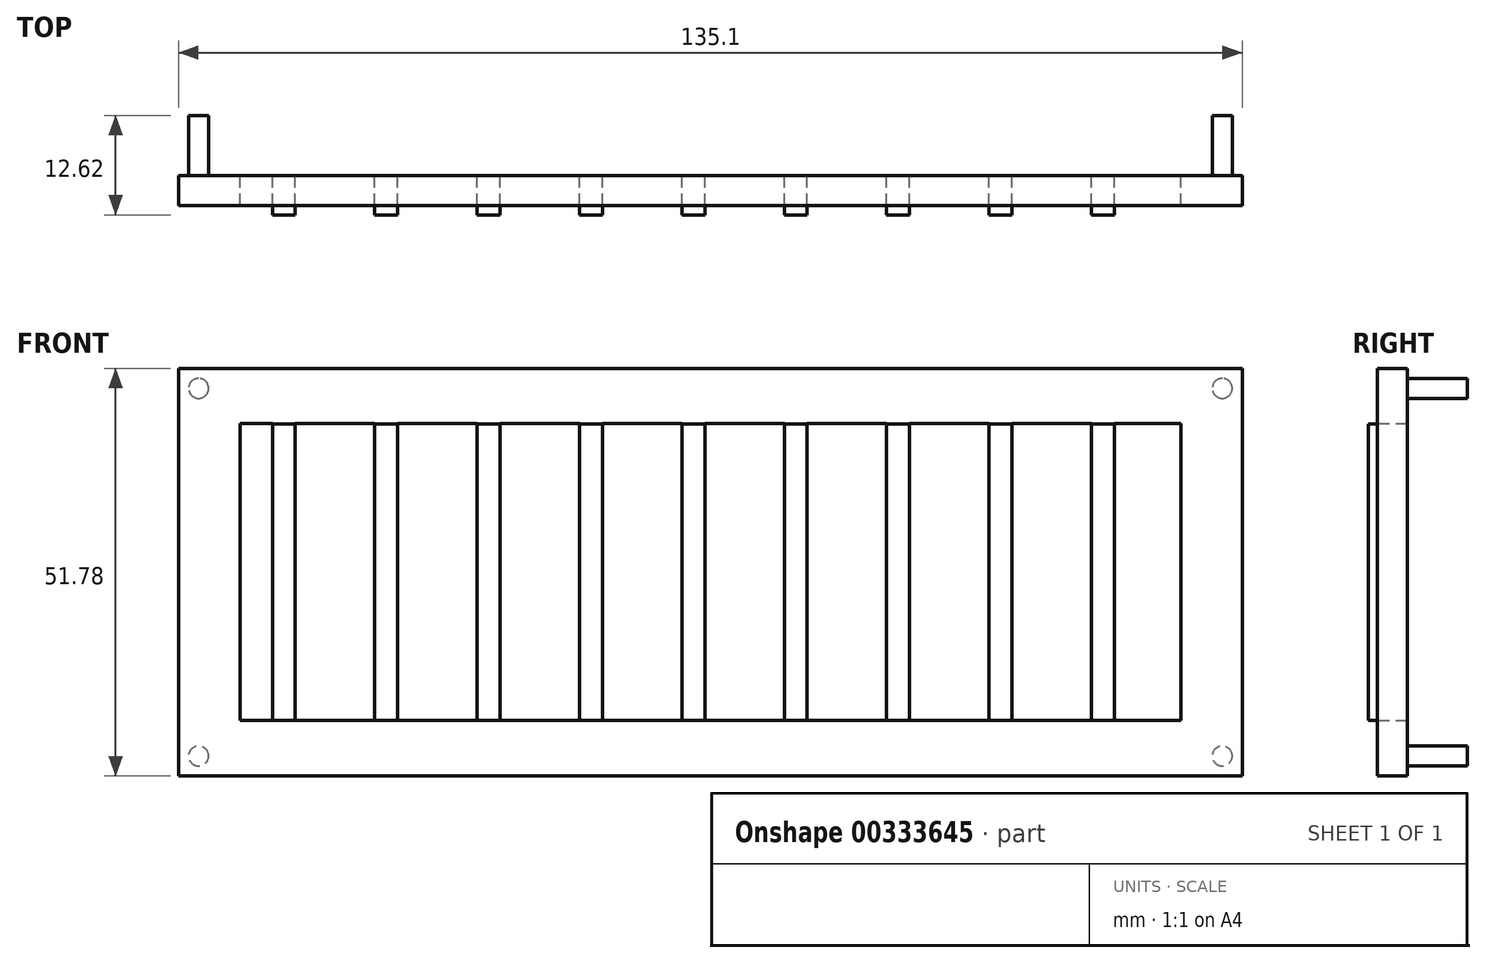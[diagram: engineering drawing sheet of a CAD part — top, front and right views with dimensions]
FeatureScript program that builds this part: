
annotation { "Feature Type Name" : "Feature", "Feature Type Description" : "" }
export const myFeature = defineFeature(function(context is Context, id is Id, definition is map)
    precondition{}
    {
        {
            var Q0;
            Q0=qCreatedBy(makeId("Front.planeOp"),FACE);
            var sketch = newSketch(context, id + "F0", { "sketchPlane" : qUnion([Q0])});
            skLineSegment(sketch, "E0.bottom", {"start": v(67.55, -25.9) * mm, "end": v(-67.55, -25.9) * mm});
            skLineSegment(sketch, "E0.top", {"start": v(67.55, 25.9) * mm, "end": v(-67.55, 25.9) * mm});
            skLineSegment(sketch, "E0.left", {"start": v(67.55, -25.9) * mm, "end": v(67.55, 25.9) * mm});
            skLineSegment(sketch, "E0.right", {"start": v(-67.55, -25.9) * mm, "end": v(-67.55, 25.9) * mm});
            skPoint(sketch, "E0.middle", {"position": v(0, 0) * mm});
            skLineSegment(sketch, "E1.bottom", {"start": v(59.76, -18.86) * mm, "end": v(-59.76, -18.86) * mm});
            skLineSegment(sketch, "E1.top", {"start": v(59.76, 18.86) * mm, "end": v(-59.76, 18.86) * mm});
            skLineSegment(sketch, "E1.left", {"start": v(59.76, -18.86) * mm, "end": v(59.76, 18.86) * mm});
            skLineSegment(sketch, "E1.right", {"start": v(-59.76, -18.86) * mm, "end": v(-59.76, 18.86) * mm});
            skSolve(sketch);
        }
        {
            var Q0;
            Q0=makeQuery(id+"F0.imprint","IMPRINT",FACE,{"disambiguationData":[TD([[makeQuery(id+"F0.imprint","IMPRINT",EDGE,{"derivedFrom":sQuery(id+"F0.wireOp",EDGE,"E1.bottom")}),-1.0]])]});
            var sketch = newSketch(context, id + "F1", { "sketchPlane" : qUnion([Q0])});
            skLineSegment(sketch, "E2", {"start": v(35.39, 18.86) * mm, "end": v(35.39, -18.88) * mm});
            skLineSegment(sketch, "E3", {"start": v(35.39, -18.88) * mm, "end": v(35.39, 18.86) * mm});
            skLineSegment(sketch, "E4", {"start": v(35.39, 18.86) * mm, "end": v(38.3, 18.86) * mm});
            skLineSegment(sketch, "E5", {"start": v(38.3, 18.86) * mm, "end": v(38.3, -18.88) * mm});
            skLineSegment(sketch, "E6", {"start": v(35.39, -18.88) * mm, "end": v(38.3, -18.88) * mm});
            skLineSegment(sketch, "E7.1.0.0", {"start": v(22.38, -18.88) * mm, "end": v(25.29, -18.88) * mm});
            skLineSegment(sketch, "E7.1.0.1", {"start": v(22.38, 18.86) * mm, "end": v(22.38, -18.88) * mm});
            skLineSegment(sketch, "E7.1.0.2", {"start": v(25.29, 18.86) * mm, "end": v(25.29, -18.88) * mm});
            skLineSegment(sketch, "E7.1.0.3", {"start": v(22.38, 18.86) * mm, "end": v(25.29, 18.86) * mm});
            skLineSegment(sketch, "E7.2.0.0", {"start": v(9.38, -18.88) * mm, "end": v(12.28, -18.88) * mm});
            skLineSegment(sketch, "E7.2.0.1", {"start": v(9.38, 18.86) * mm, "end": v(9.38, -18.88) * mm});
            skLineSegment(sketch, "E7.2.0.2", {"start": v(12.28, 18.86) * mm, "end": v(12.28, -18.88) * mm});
            skLineSegment(sketch, "E7.2.0.3", {"start": v(9.38, 18.86) * mm, "end": v(12.28, 18.86) * mm});
            skLineSegment(sketch, "E7.3.0.0", {"start": v(-3.63, -18.88) * mm, "end": v(-0.72, -18.88) * mm});
            skLineSegment(sketch, "E7.3.0.1", {"start": v(-3.63, 18.86) * mm, "end": v(-3.63, -18.88) * mm});
            skLineSegment(sketch, "E7.3.0.2", {"start": v(-0.72, 18.86) * mm, "end": v(-0.72, -18.88) * mm});
            skLineSegment(sketch, "E7.3.0.3", {"start": v(-3.63, 18.86) * mm, "end": v(-0.72, 18.86) * mm});
            skLineSegment(sketch, "E7.4.0.0", {"start": v(-16.63, -18.88) * mm, "end": v(-13.73, -18.88) * mm});
            skLineSegment(sketch, "E7.4.0.1", {"start": v(-16.63, 18.86) * mm, "end": v(-16.63, -18.88) * mm});
            skLineSegment(sketch, "E7.4.0.2", {"start": v(-13.73, 18.86) * mm, "end": v(-13.73, -18.88) * mm});
            skLineSegment(sketch, "E7.4.0.3", {"start": v(-16.63, 18.86) * mm, "end": v(-13.73, 18.86) * mm});
            skLineSegment(sketch, "E7.5.0.0", {"start": v(-29.64, -18.88) * mm, "end": v(-26.73, -18.88) * mm});
            skLineSegment(sketch, "E7.5.0.1", {"start": v(-29.64, 18.86) * mm, "end": v(-29.64, -18.88) * mm});
            skLineSegment(sketch, "E7.5.0.2", {"start": v(-26.73, 18.86) * mm, "end": v(-26.73, -18.88) * mm});
            skLineSegment(sketch, "E7.5.0.3", {"start": v(-29.64, 18.86) * mm, "end": v(-26.73, 18.86) * mm});
            skLineSegment(sketch, "E7.6.0.0", {"start": v(-42.64, -18.88) * mm, "end": v(-39.74, -18.88) * mm});
            skLineSegment(sketch, "E7.6.0.1", {"start": v(-42.64, 18.86) * mm, "end": v(-42.64, -18.88) * mm});
            skLineSegment(sketch, "E7.6.0.2", {"start": v(-39.74, 18.86) * mm, "end": v(-39.74, -18.88) * mm});
            skLineSegment(sketch, "E7.6.0.3", {"start": v(-42.64, 18.86) * mm, "end": v(-39.74, 18.86) * mm});
            skLineSegment(sketch, "E7.7.0.0", {"start": v(-55.65, -18.88) * mm, "end": v(-52.74, -18.88) * mm});
            skLineSegment(sketch, "E7.7.0.1", {"start": v(-55.65, 18.86) * mm, "end": v(-55.65, -18.88) * mm});
            skLineSegment(sketch, "E7.7.0.2", {"start": v(-52.74, 18.86) * mm, "end": v(-52.74, -18.88) * mm});
            skLineSegment(sketch, "E7.7.0.3", {"start": v(-55.65, 18.86) * mm, "end": v(-52.74, 18.86) * mm});
            skLineSegment(sketch, "E7.direction1", {"start": v(38.3, -18.88) * mm, "end": v(25.29, -18.88) * mm, "construction": true});
            skLineSegment(sketch, "E8.direction1", {"start": v(38.3, -18.88) * mm, "end": v(63.7, -18.88) * mm, "construction": true});
            skLineSegment(sketch, "E9.1.0.0", {"start": v(48.4, -18.88) * mm, "end": v(51.3, -18.88) * mm});
            skLineSegment(sketch, "E9.1.0.1", {"start": v(48.4, 18.86) * mm, "end": v(48.4, -18.88) * mm});
            skLineSegment(sketch, "E9.1.0.2", {"start": v(51.3, 18.86) * mm, "end": v(51.3, -18.88) * mm});
            skLineSegment(sketch, "E9.1.0.3", {"start": v(48.4, 18.86) * mm, "end": v(51.3, 18.86) * mm});
            skLineSegment(sketch, "E9.direction1", {"start": v(38.3, -18.88) * mm, "end": v(51.3, -18.88) * mm, "construction": true});
            skSolve(sketch);
        }
        {
            var Q0;
            Q0=makeQuery(id+"F0.imprint","IMPRINT",FACE,{"disambiguationData":[TD([[makeQuery(id+"F0.imprint","IMPRINT",EDGE,{"derivedFrom":sQuery(id+"F0.wireOp",EDGE,"E0.bottom")}),-1.0]])]});
            extrude(context, id + "F2", {"entities" : qUnion([Q0]), "depth" : 3.8 * mm});
        }
        {
            var Q0;
            {var subQ0=sQuery(id+"F1.wireOp",EDGE,"E7.7.0.3");Q0=makeQuery(id+"F1.imprint","IMPRINT",FACE,{"disambiguationData":[TD([[makeQuery(id+"F1.imprint","IMPRINT",EDGE,{"derivedFrom":subQ0}),-1.0]])]});}
            var Q1;
            {var subQ0=sQuery(id+"F1.wireOp",EDGE,"E7.6.0.3");Q1=makeQuery(id+"F1.imprint","IMPRINT",FACE,{"disambiguationData":[TD([[makeQuery(id+"F1.imprint","IMPRINT",EDGE,{"derivedFrom":subQ0}),-1.0]])]});}
            var Q2;
            {var subQ0=sQuery(id+"F1.wireOp",EDGE,"E7.5.0.3");Q2=makeQuery(id+"F1.imprint","IMPRINT",FACE,{"disambiguationData":[TD([[makeQuery(id+"F1.imprint","IMPRINT",EDGE,{"derivedFrom":subQ0}),-1.0]])]});}
            var Q3;
            {var subQ0=sQuery(id+"F1.wireOp",EDGE,"E7.4.0.3");Q3=makeQuery(id+"F1.imprint","IMPRINT",FACE,{"disambiguationData":[TD([[makeQuery(id+"F1.imprint","IMPRINT",EDGE,{"derivedFrom":subQ0}),-1.0]])]});}
            var Q4;
            {var subQ0=sQuery(id+"F1.wireOp",EDGE,"E7.3.0.3");Q4=makeQuery(id+"F1.imprint","IMPRINT",FACE,{"disambiguationData":[TD([[makeQuery(id+"F1.imprint","IMPRINT",EDGE,{"derivedFrom":subQ0}),-1.0]])]});}
            var Q5;
            {var subQ0=sQuery(id+"F1.wireOp",EDGE,"E7.2.0.3");Q5=makeQuery(id+"F1.imprint","IMPRINT",FACE,{"disambiguationData":[TD([[makeQuery(id+"F1.imprint","IMPRINT",EDGE,{"derivedFrom":subQ0}),-1.0]])]});}
            var Q6;
            {var subQ0=sQuery(id+"F1.wireOp",EDGE,"E7.1.0.3");Q6=makeQuery(id+"F1.imprint","IMPRINT",FACE,{"disambiguationData":[TD([[makeQuery(id+"F1.imprint","IMPRINT",EDGE,{"derivedFrom":subQ0}),-1.0]])]});}
            var Q7;
            {var subQ0=sQuery(id+"F1.wireOp",EDGE,"E4");Q7=makeQuery(id+"F1.imprint","IMPRINT",FACE,{"disambiguationData":[TD([[makeQuery(id+"F1.imprint","IMPRINT",EDGE,{"derivedFrom":subQ0}),-1.0]])]});}
            var Q8;
            {var subQ0=sQuery(id+"F1.wireOp",EDGE,"E9.1.0.3");Q8=makeQuery(id+"F1.imprint","IMPRINT",FACE,{"disambiguationData":[TD([[makeQuery(id+"F1.imprint","IMPRINT",EDGE,{"derivedFrom":subQ0}),-1.0]])]});}
            extrude(context, id + "F3", {"entities" : qUnion([Q0, Q1, Q2, Q3, Q4, Q5, Q6, Q7, Q8]), "operationType" : NewBodyOperationType.ADD, "depth" : 5 * mm});
        }
        {
            var Q0;
            {var subQ0=sQuery(id+"F0.wireOp",EDGE,"E1.bottom");Q0=makeQuery(id+"F3.boolean.opBoolean","MERGE",FACE,{"derivedFrom":[makeQuery(id+"F2.opExtrude","CAP_FACE",FACE,{"disambiguationData":[OSD([sQuery(id+"F0.wireOp",EDGE,"E0.bottom"),sQuery(id+"F0.wireOp",EDGE,"E0.top"),sQuery(id+"F0.wireOp",EDGE,"E0.left"),sQuery(id+"F0.wireOp",EDGE,"E0.right"),subQ0,sQuery(id+"F0.wireOp",EDGE,"E1.top"),sQuery(id+"F0.wireOp",EDGE,"E1.left"),sQuery(id+"F0.wireOp",EDGE,"E1.right")])],"isStart":true}),makeQuery(id+"F3.opExtrude","CAP_FACE",FACE,{"disambiguationData":[OSD([subQ0,sQuery(id+"F1.wireOp",EDGE,"E3"),sQuery(id+"F1.wireOp",EDGE,"E4"),sQuery(id+"F1.wireOp",EDGE,"E5")])],"isStart":true}),makeQuery(id+"F3.opExtrude","CAP_FACE",FACE,{"disambiguationData":[OSD([subQ0,sQuery(id+"F1.wireOp",EDGE,"E7.1.0.1"),sQuery(id+"F1.wireOp",EDGE,"E7.1.0.2"),sQuery(id+"F1.wireOp",EDGE,"E7.1.0.3")])],"isStart":true}),makeQuery(id+"F3.opExtrude","CAP_FACE",FACE,{"disambiguationData":[OSD([subQ0,sQuery(id+"F1.wireOp",EDGE,"E7.2.0.1"),sQuery(id+"F1.wireOp",EDGE,"E7.2.0.2"),sQuery(id+"F1.wireOp",EDGE,"E7.2.0.3")])],"isStart":true}),makeQuery(id+"F3.opExtrude","CAP_FACE",FACE,{"disambiguationData":[OSD([subQ0,sQuery(id+"F1.wireOp",EDGE,"E7.3.0.1"),sQuery(id+"F1.wireOp",EDGE,"E7.3.0.2"),sQuery(id+"F1.wireOp",EDGE,"E7.3.0.3")])],"isStart":true}),makeQuery(id+"F3.opExtrude","CAP_FACE",FACE,{"disambiguationData":[OSD([subQ0,sQuery(id+"F1.wireOp",EDGE,"E7.4.0.1"),sQuery(id+"F1.wireOp",EDGE,"E7.4.0.2"),sQuery(id+"F1.wireOp",EDGE,"E7.4.0.3")])],"isStart":true}),makeQuery(id+"F3.opExtrude","CAP_FACE",FACE,{"disambiguationData":[OSD([subQ0,sQuery(id+"F1.wireOp",EDGE,"E7.5.0.1"),sQuery(id+"F1.wireOp",EDGE,"E7.5.0.2"),sQuery(id+"F1.wireOp",EDGE,"E7.5.0.3")])],"isStart":true}),makeQuery(id+"F3.opExtrude","CAP_FACE",FACE,{"disambiguationData":[OSD([subQ0,sQuery(id+"F1.wireOp",EDGE,"E7.6.0.1"),sQuery(id+"F1.wireOp",EDGE,"E7.6.0.2"),sQuery(id+"F1.wireOp",EDGE,"E7.6.0.3")])],"isStart":true}),makeQuery(id+"F3.opExtrude","CAP_FACE",FACE,{"disambiguationData":[OSD([subQ0,sQuery(id+"F1.wireOp",EDGE,"E7.7.0.1"),sQuery(id+"F1.wireOp",EDGE,"E7.7.0.2"),sQuery(id+"F1.wireOp",EDGE,"E7.7.0.3")])],"isStart":true}),makeQuery(id+"F3.opExtrude","CAP_FACE",FACE,{"disambiguationData":[OSD([subQ0,sQuery(id+"F1.wireOp",EDGE,"E9.1.0.1"),sQuery(id+"F1.wireOp",EDGE,"E9.1.0.2"),sQuery(id+"F1.wireOp",EDGE,"E9.1.0.3")])],"isStart":true})]});}
            var sketch = newSketch(context, id + "F4", { "sketchPlane" : qUnion([Q0])});
            skCircle(sketch, "E10", {"center": v(65.01, 23.35) * mm, "radius": 1.27 * mm});
            skSolve(sketch);
        }
        {
            var Q0;
            Q0=makeQuery(id+"F4.imprint","IMPRINT",FACE,{"disambiguationData":[TD([[makeQuery(id+"F4.imprint","IMPRINT",EDGE,{"derivedFrom":sQuery(id+"F4.wireOp",EDGE,"E10")}),1.0]])]});
            extrude(context, id + "F5", {"entities" : qUnion([Q0]), "depth" : 7.62 * mm});
        }
        {
            var Q0;
            Q0=makeQuery(id+"F5.opExtrude","SWEPT_BODY",BODY,{"disambiguationData":[OSD([sQuery(id+"F4.wireOp",EDGE,"E10")])]});
            var Q1;
            Q1=qCreatedBy(makeId("Right.planeOp"),FACE);
            mirror(context, id + "F6", {"entities" : qUnion([Q0]), "mirrorPlane" : qUnion([Q1])});
        }
        {
            var Q0;
            Q0=makeQuery(id+"F5.opExtrude","SWEPT_BODY",BODY,{"disambiguationData":[OSD([sQuery(id+"F4.wireOp",EDGE,"E10")])]});
            var Q1;
            Q1=makeQuery(id+"F6.opPattern","COPY",BODY,{"derivedFrom":makeQuery(id+"F5.opExtrude","SWEPT_BODY",BODY,{"disambiguationData":[OSD([sQuery(id+"F4.wireOp",EDGE,"E10")])]}),"instanceName":"1"});
            var Q2;
            Q2=qCreatedBy(makeId("Top.planeOp"),FACE);
            mirror(context, id + "F7", {"operationType" : NewBodyOperationType.ADD, "entities" : qUnion([Q0, Q1]), "mirrorPlane" : qUnion([Q2])});
        }
        {
            var Q0;
            Q0=qCreatedBy(makeId("Front.planeOp"),FACE);
            var sketch = newSketch(context, id + "F8", { "sketchPlane" : qUnion([Q0])});
            skLineSegment(sketch, "E11.bottom", {"start": v(88.9, 50.8) * mm, "end": v(-88.9, 50.8) * mm});
            skLineSegment(sketch, "E11.top", {"start": v(88.9, -50.8) * mm, "end": v(-88.9, -50.8) * mm});
            skLineSegment(sketch, "E11.left", {"start": v(88.9, 50.8) * mm, "end": v(88.9, -50.8) * mm});
            skLineSegment(sketch, "E11.right", {"start": v(-88.9, 50.8) * mm, "end": v(-88.9, -50.8) * mm});
            skPoint(sketch, "E11.middle", {"position": v(0, 0) * mm});
            skLineSegment(sketch, "E12", {"start": v(88.9, 0) * mm, "end": v(-88.9, 0) * mm});
            skCircle(sketch, "E13", {"center": v(88.9, 50.8) * mm, "radius": 3.18 * mm});
            skCircle(sketch, "E14", {"center": v(-88.9, 50.8) * mm, "radius": 3.18 * mm});
            skSolve(sketch);
        }
        {
            var Q0;
            Q0=qCreatedBy(makeId("Top.planeOp"),FACE);
            cPlane(context, id + "F9", {"entities" : qUnion([Q0]), "cplaneType" : CPlaneType.OFFSET, "offset" : 54.6 * mm, "width" : 152.4 * mm, "height" : 152.4 * mm});
        }
        {
            var Q0;
            Q0=qCreatedBy(id+"F9.planeOp",FACE);
            var sketch = newSketch(context, id + "F10", { "sketchPlane" : qUnion([Q0])});
            skPoint(sketch, "E15.0", {"position": v(88.9, 0) * mm});
            skPoint(sketch, "E16.0", {"position": v(-88.9, 0) * mm});
            skLineSegment(sketch, "E17", {"start": v(-88.9, 0) * mm, "end": v(-63.5, 25.4) * mm});
            skLineSegment(sketch, "E18", {"start": v(-63.5, 25.4) * mm, "end": v(63.5, 25.4) * mm});
            skLineSegment(sketch, "E19", {"start": v(63.5, 25.4) * mm, "end": v(88.9, 0) * mm});
            skLineSegment(sketch, "E20", {"start": v(-88.9, 0) * mm, "end": v(88.9, 0) * mm});
            skSolve(sketch);
        }
        {
            var Q0;
            {var subQ0=sQuery(id+"F8.wireOp",EDGE,"E11.left");var subQ1=sQuery(id+"F8.wireOp",EDGE,"E11.bottom");var subQ2=makeQuery(id+"F8.imprint","INTERSECT",VERTEX,{"derivedFrom":[subQ1,subQ0]});Q0=makeQuery(id+"F8.imprint","IMPRINT",FACE,{"disambiguationData":[TD([[makeQuery(id+"F8.imprint","IMPRINT",EDGE,{"disambiguationData":[TD([[subQ2,-1.0]])],"derivedFrom":subQ1}),-1.0]])]});}
            var Q1;
            {var subQ0=sQuery(id+"F8.wireOp",EDGE,"E11.left");var subQ1=sQuery(id+"F8.wireOp",EDGE,"E11.bottom");var subQ2=makeQuery(id+"F8.imprint","INTERSECT",VERTEX,{"derivedFrom":[subQ1,subQ0]});Q1=makeQuery(id+"F8.imprint","IMPRINT",FACE,{"disambiguationData":[TD([[makeQuery(id+"F8.imprint","IMPRINT",EDGE,{"disambiguationData":[TD([[subQ2,-1.0]])],"derivedFrom":subQ1}),1.0]])]});}
            var Q2;
            Q2=sQuery(id+"F10.wireOp",EDGE,"E19");
            var Q3;
            Q3=sQuery(id+"F10.wireOp",EDGE,"E18");
            sweep(context, id + "F11", {"profiles" : qUnion([Q0, Q1]), "path" : qUnion([Q2, Q3])});
        }
        {
            var Q0;
            {var subQ0=sQuery(id+"F8.wireOp",EDGE,"E11.right");var subQ1=sQuery(id+"F8.wireOp",EDGE,"E11.bottom");var subQ2=makeQuery(id+"F8.imprint","INTERSECT",VERTEX,{"derivedFrom":[subQ1,subQ0]});Q0=makeQuery(id+"F8.imprint","IMPRINT",FACE,{"disambiguationData":[TD([[makeQuery(id+"F8.imprint","IMPRINT",EDGE,{"disambiguationData":[TD([[subQ2,1.0]])],"derivedFrom":subQ1}),-1.0]])]});}
            var Q1;
            {var subQ0=sQuery(id+"F8.wireOp",EDGE,"E11.right");var subQ1=sQuery(id+"F8.wireOp",EDGE,"E11.bottom");var subQ2=makeQuery(id+"F8.imprint","INTERSECT",VERTEX,{"derivedFrom":[subQ1,subQ0]});Q1=makeQuery(id+"F8.imprint","IMPRINT",FACE,{"disambiguationData":[TD([[makeQuery(id+"F8.imprint","IMPRINT",EDGE,{"disambiguationData":[TD([[subQ2,1.0]])],"derivedFrom":subQ1}),1.0]])]});}
            var Q2;
            Q2=sQuery(id+"F10.wireOp",EDGE,"E17");
            var Q3;
            Q3=sQuery(id+"F10.wireOp",EDGE,"E18");
            sweep(context, id + "F12", {"operationType" : NewBodyOperationType.ADD, "profiles" : qUnion([Q0, Q1]), "path" : qUnion([Q2, Q3])});
        }
        {
            var Q0;
            Q0=makeQuery(id+"F11.opSweep","SWEPT_BODY",BODY,{"disambiguationData":[OSD([sQuery(id+"F8.wireOp",EDGE,"E13"),sQuery(id+"F10.wireOp",EDGE,"E18")])]});
            deleteBodies(context, id + "F13", {"entities" : qUnion([Q0])});
        }
    });
